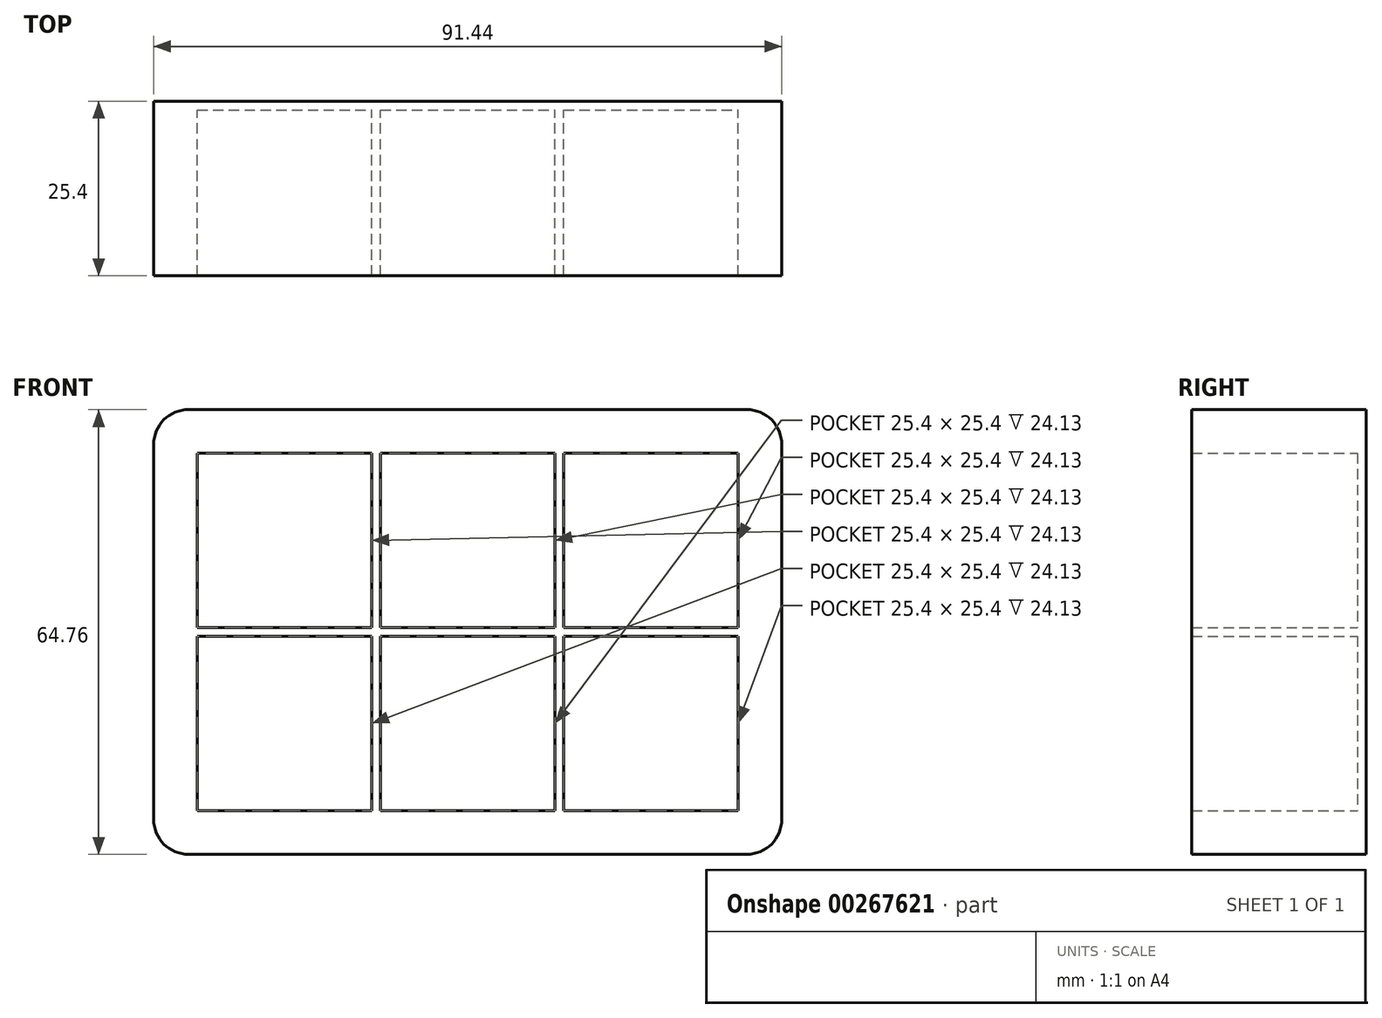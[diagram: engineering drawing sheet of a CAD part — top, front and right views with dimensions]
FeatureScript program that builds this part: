
annotation { "Feature Type Name" : "Feature", "Feature Type Description" : "" }
export const myFeature = defineFeature(function(context is Context, id is Id, definition is map)
    precondition{}
    {
        {
            var Q0;
            Q0=qCreatedBy(makeId("Front.planeOp"),FACE);
            var sketch = newSketch(context, id + "F0", { "sketchPlane" : qUnion([Q0])});
            skLineSegment(sketch, "E0.bottom", {"start": v(45.72, -32.39) * mm, "end": v(-45.72, -32.39) * mm});
            skLineSegment(sketch, "E0.top", {"start": v(45.72, 32.39) * mm, "end": v(-45.72, 32.38) * mm});
            skLineSegment(sketch, "E0.left", {"start": v(45.72, -32.39) * mm, "end": v(45.72, 32.39) * mm});
            skLineSegment(sketch, "E0.right", {"start": v(-45.72, -32.39) * mm, "end": v(-45.72, 32.38) * mm});
            skPoint(sketch, "E0.middle", {"position": v(0, 0) * mm});
            skLineSegment(sketch, "E1", {"start": v(-45.72, 27.4) * mm, "end": v(-39.37, 27.4) * mm});
            skLineSegment(sketch, "E2", {"start": v(-38.43, 32.38) * mm, "end": v(-38.43, 26.03) * mm});
            skLineSegment(sketch, "E3.bottom", {"start": v(-39.37, 26.03) * mm, "end": v(-13.97, 26.03) * mm});
            skLineSegment(sketch, "E3.top", {"start": v(-39.37, 0.63) * mm, "end": v(-13.97, 0.63) * mm});
            skLineSegment(sketch, "E3.left", {"start": v(-39.37, 26.03) * mm, "end": v(-39.37, 0.63) * mm});
            skLineSegment(sketch, "E3.right", {"start": v(-13.97, 26.03) * mm, "end": v(-13.97, 0.63) * mm});
            skLineSegment(sketch, "E4", {"start": v(-36.46, 0.63) * mm, "end": v(-36.46, -0.64) * mm});
            skLineSegment(sketch, "E5.bottom", {"start": v(-39.37, -0.64) * mm, "end": v(-13.97, -0.64) * mm});
            skLineSegment(sketch, "E5.top", {"start": v(-39.37, -26.04) * mm, "end": v(-13.97, -26.04) * mm});
            skLineSegment(sketch, "E5.left", {"start": v(-39.37, -0.64) * mm, "end": v(-39.37, -26.04) * mm});
            skLineSegment(sketch, "E5.right", {"start": v(-13.97, -0.64) * mm, "end": v(-13.97, -26.04) * mm});
            skLineSegment(sketch, "E6", {"start": v(-13.97, 13.33) * mm, "end": v(-12.7, 13.33) * mm});
            skLineSegment(sketch, "E7.bottom", {"start": v(-12.7, 26.03) * mm, "end": v(12.7, 26.03) * mm});
            skLineSegment(sketch, "E7.top", {"start": v(-12.7, 0.63) * mm, "end": v(12.7, 0.63) * mm});
            skLineSegment(sketch, "E7.left", {"start": v(-12.7, 26.03) * mm, "end": v(-12.7, 0.63) * mm});
            skLineSegment(sketch, "E7.right", {"start": v(12.7, 26.04) * mm, "end": v(12.7, 0.63) * mm});
            skLineSegment(sketch, "E8.bottom", {"start": v(-12.7, -0.64) * mm, "end": v(12.7, -0.64) * mm});
            skLineSegment(sketch, "E8.top", {"start": v(-12.7, -26.04) * mm, "end": v(12.7, -26.04) * mm});
            skLineSegment(sketch, "E8.left", {"start": v(-12.7, -0.64) * mm, "end": v(-12.7, -26.04) * mm});
            skLineSegment(sketch, "E8.right", {"start": v(12.7, -0.64) * mm, "end": v(12.7, -26.04) * mm});
            skLineSegment(sketch, "E9", {"start": v(12.7, 15.57) * mm, "end": v(13.97, 15.57) * mm});
            skLineSegment(sketch, "E10.bottom", {"start": v(13.97, 26.03) * mm, "end": v(39.37, 26.03) * mm});
            skLineSegment(sketch, "E10.top", {"start": v(13.97, 0.63) * mm, "end": v(39.37, 0.63) * mm});
            skLineSegment(sketch, "E10.left", {"start": v(13.97, 26.03) * mm, "end": v(13.97, 0.63) * mm});
            skLineSegment(sketch, "E10.right", {"start": v(39.37, 26.04) * mm, "end": v(39.37, 0.63) * mm});
            skLineSegment(sketch, "E11.bottom", {"start": v(13.97, -0.64) * mm, "end": v(39.37, -0.64) * mm});
            skLineSegment(sketch, "E11.top", {"start": v(13.97, -26.04) * mm, "end": v(39.37, -26.04) * mm});
            skLineSegment(sketch, "E11.left", {"start": v(13.97, -0.64) * mm, "end": v(13.97, -26.04) * mm});
            skLineSegment(sketch, "E11.right", {"start": v(39.37, -0.64) * mm, "end": v(39.37, -26.04) * mm});
            skSolve(sketch);
        }
        {
            var Q0;
            {var subQ26=sQuery(id+"F0.wireOp",EDGE,"E0.bottom");Q0=makeQuery(id+"F0.imprint","IMPRINT",FACE,{"disambiguationData":[TD([[makeQuery(id+"F0.imprint","IMPRINT",EDGE,{"derivedFrom":subQ26}),-1.0]])]});}
            extrude(context, id + "F1", {"entities" : qUnion([Q0]), "depth" : 25.4 * mm});
        }
        {
            var Q0;
            Q0=qCreatedBy(makeId("Front.planeOp"),FACE);
            var sketch = newSketch(context, id + "F2", { "sketchPlane" : qUnion([Q0])});
            skLineSegment(sketch, "E12.bottom", {"start": v(-45.72, -32.39) * mm, "end": v(45.72, -32.39) * mm});
            skLineSegment(sketch, "E12.top", {"start": v(-45.72, 32.38) * mm, "end": v(45.72, 32.38) * mm});
            skLineSegment(sketch, "E12.left", {"start": v(-45.72, -32.39) * mm, "end": v(-45.72, 32.38) * mm});
            skLineSegment(sketch, "E12.right", {"start": v(45.72, -32.39) * mm, "end": v(45.72, 32.38) * mm});
            skPoint(sketch, "E12.middle", {"position": v(0, 0) * mm});
            skSolve(sketch);
        }
        {
            var Q0;
            Q0=makeQuery(id+"F2.imprint","IMPRINT",FACE,{"disambiguationData":[TD([[makeQuery(id+"F2.imprint","IMPRINT",EDGE,{"derivedFrom":sQuery(id+"F2.wireOp",EDGE,"E12.bottom")}),1.0]])]});
            extrude(context, id + "F3", {"entities" : qUnion([Q0]), "operationType" : NewBodyOperationType.ADD, "depth" : 1.27 * mm});
        }
        {
            var Q0;
            Q0=makeQuery(id+"F1.opExtrude","SWEPT_EDGE",EDGE,{"disambiguationData":[OSD([sQuery(id+"F0.wireOp",EDGE,"E0.top"),sQuery(id+"F0.wireOp",EDGE,"E0.right")])]});
            var Q1;
            Q1=makeQuery(id+"F1.opExtrude","SWEPT_EDGE",EDGE,{"disambiguationData":[OSD([sQuery(id+"F0.wireOp",EDGE,"E0.top"),sQuery(id+"F0.wireOp",EDGE,"E0.left")])]});
            var Q2;
            Q2=makeQuery(id+"F1.opExtrude","SWEPT_EDGE",EDGE,{"disambiguationData":[OSD([sQuery(id+"F0.wireOp",EDGE,"E0.bottom"),sQuery(id+"F0.wireOp",EDGE,"E0.right")])]});
            var Q3;
            Q3=makeQuery(id+"F1.opExtrude","SWEPT_EDGE",EDGE,{"disambiguationData":[OSD([sQuery(id+"F0.wireOp",EDGE,"E0.bottom"),sQuery(id+"F0.wireOp",EDGE,"E0.left")])]});
            fillet(context, id + "F4", {"entities" : qUnion([Q0, Q1, Q2, Q3]), "radius" : 5.08 * mm, "tangentPropagation" : true, "allowEdgeOverflow" : false});
        }
    });
